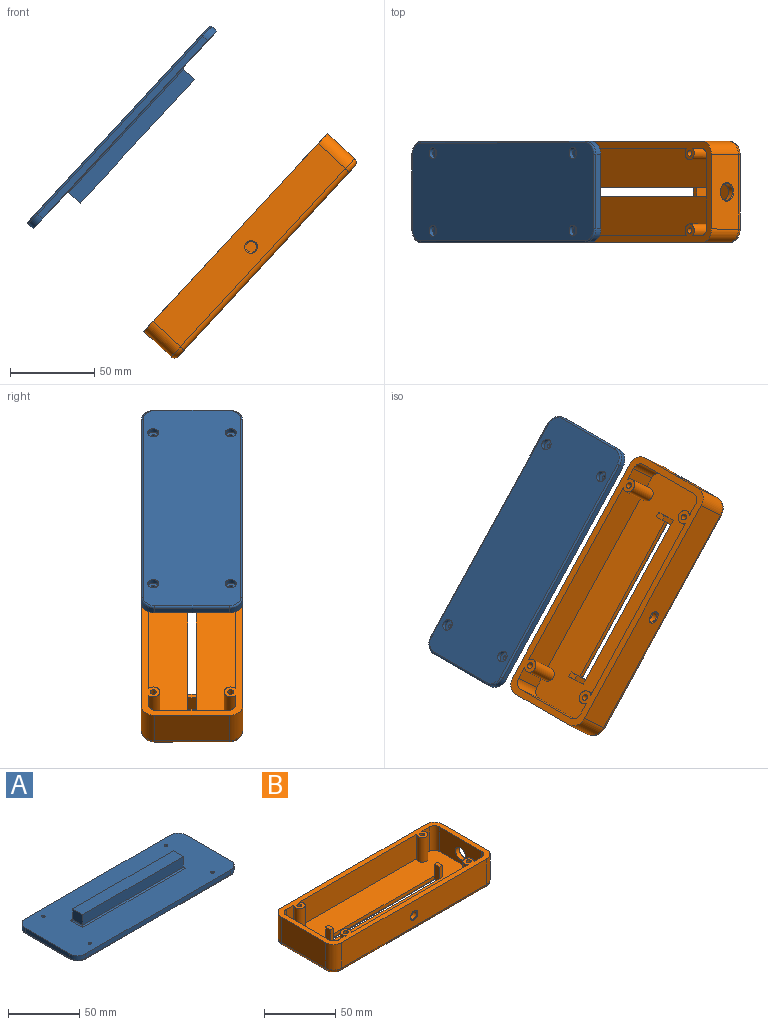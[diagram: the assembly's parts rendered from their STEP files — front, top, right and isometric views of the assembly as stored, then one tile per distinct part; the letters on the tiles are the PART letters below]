
ASSEMBLY  parts=2 mates=2
PART A: 39 faces, bbox 161.3x61.3x15 mm
  f0: cylinder r=1.2mm len=2.4mm, axis (0,0,1), area 15.1mm2, adj f4,f38
  f1: cylinder r=1.2mm len=2.4mm, axis (0,0,1), area 15.1mm2, adj f4,f36
  f2: cylinder r=1.2mm len=2.4mm, axis (0,0,1), area 15.1mm2, adj f4,f34
  f3: cylinder r=1.2mm len=2.4mm, axis (0,0,1), area 15.1mm2, adj f4,f32
  f4: plane 160x60mm, normal (0,0,1), area 8303mm2, adj f0,f1,f2,f3,f5,f6,f7,f8
  f5: plane 44x4mm, normal (1,0,0), area 176mm2, adj f4,f6,f12,f26
  f6: cylinder r=8mm len=8mm, axis (0,0,-1), area 50.3mm2, adj f4,f5,f7,f24
  f7: plane 144x4mm, normal (0,1,0), area 576mm2, adj f4,f6,f8,f22
  f8: cylinder r=8mm len=8mm, axis (0,0,-1), area 50.3mm2, adj f4,f7,f9,f20
  f9: plane 44x4mm, normal (-1,0,0), area 176mm2, adj f4,f8,f10,f19
  f10: cylinder r=8mm len=8mm, axis (0,0,-1), area 50.3mm2, adj f4,f9,f11,f21
  f11: plane 144x4mm, normal (0,-1,0), area 576mm2, adj f4,f10,f12,f23
  f12: cylinder r=8mm len=8mm, axis (0,0,-1), area 50.3mm2, adj f4,f5,f11,f25
  f13: plane 158x58mm, normal (0,0,-1), area 8989.2mm2, adj f19,f20,f21,f22,f23,f24,f25,f26
  f14: plane 100x9mm, normal (0,1,0), area 900mm2, adj f15,f17,f18,f27
  f15: plane 10x9mm, normal (-1,0,0), area 90mm2, adj f14,f16,f18,f28
  f16: plane 100x9mm, normal (0,-1,0), area 900mm2, adj f15,f17,f18,f30
  f17: plane 10x9mm, normal (1,0,0), area 90mm2, adj f14,f16,f18,f29
  f18: plane 100x10mm, normal (0,0,1), area 1000mm2, adj f14,f15,f16,f17
  f19: cylinder r=1mm len=44mm, axis (0,-1,0), area 69.1mm2, adj f9,f13,f20,f21
  f20: torus R=7mm, axis (0,0,1), area 18.8mm2, adj f8,f13,f19,f22
  f21: torus R=7mm, axis (0,0,1), area 18.8mm2, adj f10,f13,f19,f23
  f22: cylinder r=1mm len=144mm, axis (-1,0,0), area 226.2mm2, adj f7,f13,f20,f24
  f23: cylinder r=1mm len=144mm, axis (1,0,0), area 226.2mm2, adj f11,f13,f21,f25
  f24: torus R=7mm, axis (0,0,1), area 18.8mm2, adj f6,f13,f22,f26
  f25: torus R=7mm, axis (0,0,1), area 18.8mm2, adj f12,f13,f23,f26
  f26: cylinder r=1mm len=44mm, axis (0,1,0), area 69.1mm2, adj f5,f13,f24,f25
  f27: cylinder r=1mm len=102mm, axis (-1,0,0), area 158.2mm2, adj f4,f14,f28,f29
  f28: cylinder r=1mm len=12mm, axis (0,-1,0), area 16.8mm2, adj f4,f15,f27,f30
  f29: cylinder r=1mm len=12mm, axis (0,1,0), area 16.8mm2, adj f4,f17,f27,f30
  f30: cylinder r=1mm len=102mm, axis (1,0,0), area 158.2mm2, adj f4,f16,f28,f29
  f31: cylinder r=3.25mm len=6.5mm, axis (0,0,-1), area 61.3mm2, adj f13,f32
  f32: plane 6.5x6.5mm, normal (0,0,-1), area 28.7mm2, adj f3,f31
  f33: cylinder r=3.25mm len=6.5mm, axis (0,0,-1), area 61.3mm2, adj f13,f34
  f34: plane 6.5x6.5mm, normal (0,0,-1), area 28.7mm2, adj f2,f33
  f35: cylinder r=3.25mm len=6.5mm, axis (0,0,-1), area 61.3mm2, adj f13,f36
  f36: plane 6.5x6.5mm, normal (0,0,-1), area 28.7mm2, adj f1,f35
  f37: cylinder r=3.25mm len=6.5mm, axis (0,0,-1), area 61.3mm2, adj f13,f38
  f38: plane 6.5x6.5mm, normal (0,0,-1), area 28.7mm2, adj f0,f37
PART B: 63 faces, bbox 161.3x61.3x25 mm
  f0: plane 152x52mm, normal (0,0,1), area 7141mm2, adj f1,f2,f3,f4,f5,f6,f25,f26
  f1: plane 116.71x21mm, normal (0,1,0), area 2417.7mm2, adj f0,f8,f41,f42,f60
  f2: plane 21x7.35mm, normal (0,1,0), area 154.4mm2, adj f0,f8,f28,f42
  f3: plane 21x7.35mm, normal (0,1,0), area 154.4mm2, adj f0,f8,f27,f41
  f4: plane 116.71x21mm, normal (0,-1,0), area 2450.9mm2, adj f0,f8,f39,f40
  f5: plane 21x7.35mm, normal (0,-1,0), area 154.4mm2, adj f0,f8,f30,f40
  f6: plane 21x7.35mm, normal (0,-1,0), area 154.4mm2, adj f0,f8,f25,f39
  f7: plane 154x54mm, normal (0,0,-1), area 7545.5mm2, adj f17,f18,f19,f20,f21,f22,f23,f24
  f8: plane 160x60mm, normal (0,0,1), area 1810.6mm2, adj f1,f2,f3,f4,f5,f6,f9,f10
  f9: plane 44x22mm, normal (1,0,0), area 873mm2, adj f8,f10,f16,f21,f62
  f10: cylinder r=8mm len=22mm, axis (0,0,-1), area 276.5mm2, adj f8,f9,f11,f19
  f11: plane 144x22mm, normal (0,1,0), area 3168mm2, adj f8,f10,f12,f17
  f12: cylinder r=8mm len=22mm, axis (0,0,-1), area 276.5mm2, adj f8,f11,f13,f18
  f13: plane 44x22mm, normal (-1,0,0), area 968mm2, adj f8,f12,f14,f20
  f14: cylinder r=8mm len=22mm, axis (0,0,-1), area 276.5mm2, adj f8,f13,f15,f22
  f15: plane 144x22mm, normal (0,-1,0), area 3123.8mm2, adj f8,f14,f16,f24,f61
  f16: cylinder r=8mm len=22mm, axis (0,0,-1), area 276.5mm2, adj f8,f9,f15,f23
  f17: cylinder r=3mm len=144mm, axis (-1,0,0), area 678.6mm2, adj f7,f11,f18,f19
  f18: torus R=5mm, axis (0,0,1), area 51.1mm2, adj f7,f12,f17,f20
  f19: torus R=5mm, axis (0,0,1), area 51.1mm2, adj f7,f10,f17,f21
  f20: cylinder r=3mm len=44mm, axis (0,-1,0), area 207.3mm2, adj f7,f13,f18,f22
  f21: cylinder r=3mm len=44mm, axis (0,1,0), area 207.3mm2, adj f7,f9,f19,f23
  f22: torus R=5mm, axis (0,0,1), area 51.1mm2, adj f7,f14,f20,f24
  f23: torus R=5mm, axis (0,0,1), area 51.1mm2, adj f7,f16,f21,f24
  f24: cylinder r=3mm len=144mm, axis (1,0,0), area 678.6mm2, adj f7,f15,f22,f23
  f25: cylinder r=5mm len=21mm, axis (0,0,1), area 164.9mm2, adj f0,f6,f8,f26
  f26: plane 42x21mm, normal (1,0,0), area 882mm2, adj f0,f8,f25,f27
  f27: cylinder r=5mm len=21mm, axis (0,0,1), area 164.9mm2, adj f0,f3,f8,f26
  f28: cylinder r=5mm len=21mm, axis (0,0,1), area 164.9mm2, adj f0,f2,f8,f29
  f29: plane 42x21mm, normal (-1,0,0), area 803.5mm2, adj f0,f8,f28,f30,f59
  f30: cylinder r=5mm len=21mm, axis (0,0,1), area 164.9mm2, adj f0,f5,f8,f29
  f31: plane 105x3mm, normal (0,-1,0), area 315mm2, adj f0,f32,f34,f38
  f32: plane 13x5mm, normal (1,0,0), area 65mm2, adj f31,f33,f36,f51,f53,f54
  f33: plane 105x3mm, normal (0,1,0), area 315mm2, adj f0,f32,f34,f35
  f34: plane 13x5mm, normal (-1,0,0), area 65mm2, adj f31,f33,f37,f55,f56,f58
  f35: cylinder r=1mm len=107mm, axis (1,0,0), area 166.1mm2, adj f7,f33,f36,f37
  f36: cylinder r=1mm len=7mm, axis (0,-1,0), area 9mm2, adj f7,f32,f35,f38
  f37: cylinder r=1mm len=7mm, axis (0,1,0), area 9mm2, adj f7,f34,f35,f38
  f38: cylinder r=1mm len=107mm, axis (-1,0,0), area 166.1mm2, adj f7,f31,f36,f37
  f39: cylinder r=4mm len=21mm, axis (0,0,-1), area 406.4mm2, adj f0,f4,f6,f8
  f40: cylinder r=4mm len=21mm, axis (0,0,-1), area 406.4mm2, adj f0,f4,f5,f8
  f41: cylinder r=4mm len=21mm, axis (0,0,-1), area 406.4mm2, adj f0,f1,f3,f8
  f42: cylinder r=4mm len=21mm, axis (0,0,-1), area 406.4mm2, adj f0,f1,f2,f8
  f43: cylinder r=1.75mm len=15mm, axis (0,0,1), area 164.9mm2, adj f8,f44
  f44: plane 3.5x3.5mm, normal (0,0,1), area 9.6mm2, adj f43
  f45: cylinder r=1.75mm len=15mm, axis (0,0,1), area 164.9mm2, adj f8,f46
  f46: plane 3.5x3.5mm, normal (0,0,1), area 9.6mm2, adj f45
  f47: cylinder r=1.75mm len=15mm, axis (0,0,1), area 164.9mm2, adj f8,f48
  f48: plane 3.5x3.5mm, normal (0,0,1), area 9.6mm2, adj f47
  f49: cylinder r=1.75mm len=15mm, axis (0,0,1), area 164.9mm2, adj f8,f50
  f50: plane 3.5x3.5mm, normal (0,0,1), area 9.6mm2, adj f49
  f51: plane 10x3mm, normal (0,1,0), area 30mm2, adj f0,f32,f52,f54
  f52: plane 10x5mm, normal (-1,0,0), area 50mm2, adj f0,f51,f53,f54
  f53: plane 10x3mm, normal (0,-1,0), area 30mm2, adj f0,f32,f52,f54
  f54: plane 5x3mm, normal (0,0,1), area 15mm2, adj f32,f51,f52,f53
  f55: plane 10x3mm, normal (0,1,0), area 30mm2, adj f0,f34,f57,f58
  f56: plane 10x3mm, normal (0,-1,0), area 30mm2, adj f0,f34,f57,f58
  f57: plane 10x5mm, normal (1,0,0), area 50mm2, adj f0,f55,f56,f58
  f58: plane 5x3mm, normal (0,0,1), area 15mm2, adj f34,f55,f56,f57
  f59: cylinder r=5mm len=10mm, axis (1,0,0), area 110mm2, adj f29,f62
  f60: cylinder r=3.25mm len=6.5mm, axis (0,-1,0), area 71.5mm2, adj f1,f61
  f61: torus R=3.75mm, axis (0,1,0), area 16.9mm2, adj f15,f60
  f62: torus R=5.5mm, axis (1,0,0), area 25.6mm2, adj f9,f59
PLACE A rot(axis=(0,1,0),132.8deg) t=(113.26,17.26,-86.89)mm fixed
PLACE B rot(axis=(0,-1,0),47.2deg) t=(200.87,17.26,-168.14)mm
MATE planar B.f15 <-> A.f11  axis (0,-1,0) through (190.59,-12.74,-158.61)mm
MATE slider A.f0 <-> B.f42  axis (0.73,0,-0.68) through (158.4,-5.74,-45.56)mm
